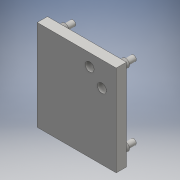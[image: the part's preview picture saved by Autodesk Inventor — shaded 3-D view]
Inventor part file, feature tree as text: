
AUTODESK INVENTOR PART (.ipt)
format: ipt  version: 2016 (Build 200138000, 138)  size: 147,456 bytes
history: native  units: mm
features: sketch x4, extrude x3, hole x1
ambient origin geometry x8: Origin, YZ Plane, XZ Plane, XY Plane, X Axis, Y Axis, Z Axis, Center Point
bodies: Solid1 (feature_tree)
feature tree (8):
  extrude  "Extrusion1"  Depth=44.5mm
  extrude  "Extrusion2"  Depth=4.0mm
  extrude  "Extrusion3"  Depth=4.5mm
  hole  "Hole1"  [1 undecoded]
  sketch  "Sketch1"  dims[d0=38.7mm d1=44.5mm]
  sketch  "Sketch2"  dims[d14=5.0mm d15=0.0mm d16=4.0mm]
  sketch  "Sketch3"  dims[d17=4.5mm d18=4.5mm]
  sketch  "Sketch4"  dims[d19=4.0mm d20=4.5mm d21=4.5mm d22=4.0mm d23=4.5mm d24=4.5mm d25=4.0mm d26=4.5mm d27=4.5mm d28=4.0mm d29=0.0mm d30=2.7mm d31=2.7mm d32=2.7mm d33=2.7mm d34=4.0mm d35=0.0mm d36=4.35mm d37=13.0mm d38=6.0mm d39=6.0mm d40=6.0mm d41=4.35mm d42=4.35mm d43=6.0mm d44=4.0mm d45=2.0mm d46=90.0deg d47=4.5mm d48=0.0mm]
note: 1 required parameter value undecoded (feature->parameter linkage not recoverable at this tier; creation-order binding heuristic only, values carry confidence <= 0.55)
